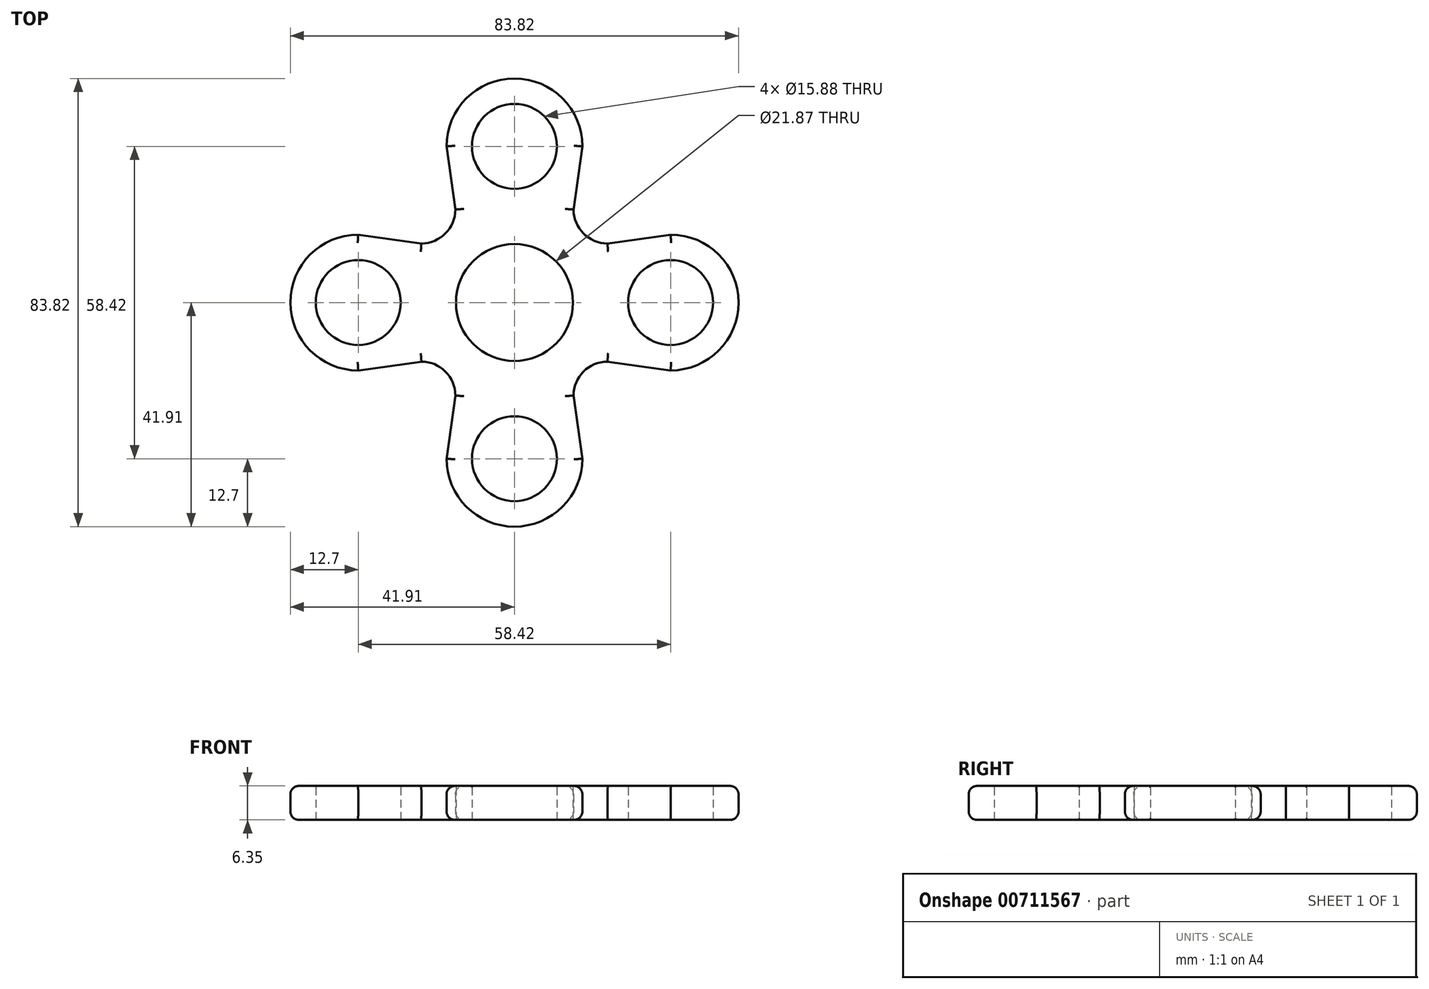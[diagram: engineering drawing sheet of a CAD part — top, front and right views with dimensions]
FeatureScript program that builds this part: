
annotation { "Feature Type Name" : "Feature", "Feature Type Description" : "" }
export const myFeature = defineFeature(function(context is Context, id is Id, definition is map)
    precondition{}
    {
        {
            var Q0;
            Q0=qCreatedBy(makeId("Top.planeOp"),FACE);
            var sketch = newSketch(context, id + "F0", { "sketchPlane" : qUnion([Q0])});
            skCircle(sketch, "E0", {"center": v(0, 0) * mm, "radius": 10.93 * mm});
            skLineSegment(sketch, "E1", {"start": v(0, 32.8) * mm, "end": v(0, -37.97) * mm, "construction": true});
            skLineSegment(sketch, "E2", {"start": v(-47.87, 0) * mm, "end": v(62.97, 0) * mm, "construction": true});
            skCircle(sketch, "E3", {"center": v(29.21, 0) * mm, "radius": 7.94 * mm});
            skCircle(sketch, "E4", {"center": v(0, 29.21) * mm, "radius": 7.94 * mm});
            skCircle(sketch, "E5", {"center": v(-29.21, 0) * mm, "radius": 7.94 * mm});
            skCircle(sketch, "E6", {"center": v(0, -29.21) * mm, "radius": 7.94 * mm});
            skArc(sketch, "E7", {"start": v(12.7, 29.2) * mm, "mid": v(0, 41.91) * mm, "end": v(-12.7, 29.21) * mm});
            skArc(sketch, "E8", {"start": v(29.2, -12.7) * mm, "mid": v(41.91, 0) * mm, "end": v(29.21, 12.7) * mm});
            skArc(sketch, "E9", {"start": v(-12.7, -29.21) * mm, "mid": v(0, -41.91) * mm, "end": v(12.7, -29.21) * mm});
            skArc(sketch, "E10", {"start": v(-29.21, 12.7) * mm, "mid": v(-41.91, 0) * mm, "end": v(-29.2, -12.7) * mm});
            skPoint(sketch, "E11.visualSharp", {"position": v(-11.05, 11.05) * mm});
            skArc(sketch, "E11.filletArc", {"start": v(-17.4, 11.05) * mm, "mid": v(-12.9, 12.9) * mm, "end": v(-11.05, 17.4) * mm});
            skPoint(sketch, "E12.visualSharp", {"position": v(11.05, 11.05) * mm});
            skArc(sketch, "E12.filletArc", {"start": v(11.05, 17.4) * mm, "mid": v(12.9, 12.9) * mm, "end": v(17.4, 11.05) * mm});
            skArc(sketch, "E13.MirrorCS", {"start": v(-17.4, -11.05) * mm, "mid": v(-12.9, -12.9) * mm, "end": v(-11.05, -17.4) * mm});
            skArc(sketch, "E14.MirrorCS", {"start": v(11.05, -17.4) * mm, "mid": v(12.9, -12.9) * mm, "end": v(17.4, -11.05) * mm});
            skLineSegment(sketch, "E15", {"start": v(-12.7, -29.21) * mm, "end": v(-11.05, -17.4) * mm});
            skLineSegment(sketch, "E16", {"start": v(12.7, -29.2) * mm, "end": v(11.05, -17.4) * mm});
            skLineSegment(sketch, "E17", {"start": v(17.4, -11.05) * mm, "end": v(29.2, -12.7) * mm});
            skLineSegment(sketch, "E18", {"start": v(17.4, 11.05) * mm, "end": v(29.2, 12.7) * mm});
            skLineSegment(sketch, "E19", {"start": v(11.05, 17.4) * mm, "end": v(12.7, 29.2) * mm});
            skLineSegment(sketch, "E20", {"start": v(-12.7, 29.21) * mm, "end": v(-11.05, 17.4) * mm});
            skLineSegment(sketch, "E21", {"start": v(-17.4, 11.05) * mm, "end": v(-29.21, 12.7) * mm});
            skLineSegment(sketch, "E22", {"start": v(-29.21, -12.7) * mm, "end": v(-17.4, -11.05) * mm});
            skSolve(sketch);
        }
        {
            var Q0;
            Q0 = qSketchRegion(id + "F0", true);
            extrude(context, id + "F1", {"entities" : qUnion([Q0]), "depth" : 6.35 * mm, "offsetDistance" : 25.4 * mm});
        }
        {
            var Q0;
            Q0=makeQuery(id+"F1.opExtrude","CAP_EDGE",EDGE,{"disambiguationData":[OSD([sQuery(id+"F0.wireOp",EDGE,"E10")])],"isStart":true});
            var Q1;
            Q1=makeQuery(id+"F1.opExtrude","CAP_EDGE",EDGE,{"disambiguationData":[OSD([sQuery(id+"F0.wireOp",EDGE,"E22")])],"isStart":true});
            var Q2;
            Q2=makeQuery(id+"F1.opExtrude","CAP_EDGE",EDGE,{"disambiguationData":[OSD([sQuery(id+"F0.wireOp",EDGE,"E13.MirrorCS")])],"isStart":true});
            var Q3;
            Q3=makeQuery(id+"F1.opExtrude","CAP_EDGE",EDGE,{"disambiguationData":[OSD([sQuery(id+"F0.wireOp",EDGE,"E15")])],"isStart":true});
            var Q4;
            Q4=makeQuery(id+"F1.opExtrude","CAP_EDGE",EDGE,{"disambiguationData":[OSD([sQuery(id+"F0.wireOp",EDGE,"E9")])],"isStart":true});
            var Q5;
            Q5=makeQuery(id+"F1.opExtrude","CAP_EDGE",EDGE,{"disambiguationData":[OSD([sQuery(id+"F0.wireOp",EDGE,"E16")])],"isStart":true});
            var Q6;
            Q6=makeQuery(id+"F1.opExtrude","CAP_EDGE",EDGE,{"disambiguationData":[OSD([sQuery(id+"F0.wireOp",EDGE,"E14.MirrorCS")])],"isStart":true});
            var Q7;
            Q7=makeQuery(id+"F1.opExtrude","CAP_EDGE",EDGE,{"disambiguationData":[OSD([sQuery(id+"F0.wireOp",EDGE,"E17")])],"isStart":true});
            var Q8;
            Q8=makeQuery(id+"F1.opExtrude","CAP_EDGE",EDGE,{"disambiguationData":[OSD([sQuery(id+"F0.wireOp",EDGE,"E8")])],"isStart":true});
            var Q9;
            Q9=makeQuery(id+"F1.opExtrude","CAP_EDGE",EDGE,{"disambiguationData":[OSD([sQuery(id+"F0.wireOp",EDGE,"E18")])],"isStart":true});
            var Q10;
            Q10=makeQuery(id+"F1.opExtrude","CAP_EDGE",EDGE,{"disambiguationData":[OSD([sQuery(id+"F0.wireOp",EDGE,"E12.filletArc")])],"isStart":true});
            var Q11;
            Q11=makeQuery(id+"F1.opExtrude","CAP_EDGE",EDGE,{"disambiguationData":[OSD([sQuery(id+"F0.wireOp",EDGE,"E19")])],"isStart":true});
            var Q12;
            Q12=makeQuery(id+"F1.opExtrude","CAP_EDGE",EDGE,{"disambiguationData":[OSD([sQuery(id+"F0.wireOp",EDGE,"E7")])],"isStart":true});
            var Q13;
            Q13=makeQuery(id+"F1.opExtrude","CAP_EDGE",EDGE,{"disambiguationData":[OSD([sQuery(id+"F0.wireOp",EDGE,"E20")])],"isStart":true});
            var Q14;
            Q14=makeQuery(id+"F1.opExtrude","CAP_EDGE",EDGE,{"disambiguationData":[OSD([sQuery(id+"F0.wireOp",EDGE,"E11.filletArc")])],"isStart":true});
            var Q15;
            Q15=makeQuery(id+"F1.opExtrude","CAP_EDGE",EDGE,{"disambiguationData":[OSD([sQuery(id+"F0.wireOp",EDGE,"E21")])],"isStart":true});
            var Q16;
            Q16=makeQuery(id+"F1.opExtrude","CAP_EDGE",EDGE,{"disambiguationData":[OSD([sQuery(id+"F0.wireOp",EDGE,"E10")])],"isStart":false});
            var Q17;
            Q17=makeQuery(id+"F1.opExtrude","CAP_EDGE",EDGE,{"disambiguationData":[OSD([sQuery(id+"F0.wireOp",EDGE,"E22")])],"isStart":false});
            var Q18;
            Q18=makeQuery(id+"F1.opExtrude","CAP_EDGE",EDGE,{"disambiguationData":[OSD([sQuery(id+"F0.wireOp",EDGE,"E13.MirrorCS")])],"isStart":false});
            var Q19;
            Q19=makeQuery(id+"F1.opExtrude","CAP_EDGE",EDGE,{"disambiguationData":[OSD([sQuery(id+"F0.wireOp",EDGE,"E21")])],"isStart":false});
            var Q20;
            Q20=makeQuery(id+"F1.opExtrude","CAP_EDGE",EDGE,{"disambiguationData":[OSD([sQuery(id+"F0.wireOp",EDGE,"E11.filletArc")])],"isStart":false});
            var Q21;
            Q21=makeQuery(id+"F1.opExtrude","CAP_EDGE",EDGE,{"disambiguationData":[OSD([sQuery(id+"F0.wireOp",EDGE,"E20")])],"isStart":false});
            var Q22;
            Q22=makeQuery(id+"F1.opExtrude","CAP_EDGE",EDGE,{"disambiguationData":[OSD([sQuery(id+"F0.wireOp",EDGE,"E7")])],"isStart":false});
            var Q23;
            Q23=makeQuery(id+"F1.opExtrude","CAP_EDGE",EDGE,{"disambiguationData":[OSD([sQuery(id+"F0.wireOp",EDGE,"E19")])],"isStart":false});
            var Q24;
            Q24=makeQuery(id+"F1.opExtrude","CAP_EDGE",EDGE,{"disambiguationData":[OSD([sQuery(id+"F0.wireOp",EDGE,"E8")])],"isStart":false});
            var Q25;
            Q25=makeQuery(id+"F1.opExtrude","CAP_EDGE",EDGE,{"disambiguationData":[OSD([sQuery(id+"F0.wireOp",EDGE,"E17")])],"isStart":false});
            var Q26;
            Q26=makeQuery(id+"F1.opExtrude","CAP_EDGE",EDGE,{"disambiguationData":[OSD([sQuery(id+"F0.wireOp",EDGE,"E14.MirrorCS")])],"isStart":false});
            var Q27;
            Q27=makeQuery(id+"F1.opExtrude","CAP_EDGE",EDGE,{"disambiguationData":[OSD([sQuery(id+"F0.wireOp",EDGE,"E16")])],"isStart":false});
            var Q28;
            Q28=makeQuery(id+"F1.opExtrude","CAP_EDGE",EDGE,{"disambiguationData":[OSD([sQuery(id+"F0.wireOp",EDGE,"E9")])],"isStart":false});
            var Q29;
            Q29=makeQuery(id+"F1.opExtrude","CAP_EDGE",EDGE,{"disambiguationData":[OSD([sQuery(id+"F0.wireOp",EDGE,"E15")])],"isStart":false});
            var Q30;
            Q30=makeQuery(id+"F1.opExtrude","CAP_EDGE",EDGE,{"disambiguationData":[OSD([sQuery(id+"F0.wireOp",EDGE,"E12.filletArc")])],"isStart":false});
            var Q31;
            Q31=makeQuery(id+"F1.opExtrude","CAP_EDGE",EDGE,{"disambiguationData":[OSD([sQuery(id+"F0.wireOp",EDGE,"E18")])],"isStart":false});
            fillet(context, id + "F2", {"entities" : qUnion([Q0, Q1, Q2, Q3, Q4, Q5, Q6, Q7, Q8, Q9, Q10, Q11, Q12, Q13, Q14, Q15, Q16, Q17, Q18, Q19, Q20, Q21, Q22, Q23, Q24, Q25, Q26, Q27, Q28, Q29, Q30, Q31]), "radius" : 1.57 * mm, "allowEdgeOverflow" : false});
        }
        {
            var Q0;
            Q0=makeQuery(id+"F1.opExtrude","CAP_EDGE",EDGE,{"disambiguationData":[OSD([sQuery(id+"F0.wireOp",EDGE,"E5")])],"isStart":false});
            var Q1;
            Q1=makeQuery(id+"F1.opExtrude","CAP_EDGE",EDGE,{"disambiguationData":[OSD([sQuery(id+"F0.wireOp",EDGE,"E4")])],"isStart":false});
            var Q2;
            Q2=makeQuery(id+"F1.opExtrude","CAP_EDGE",EDGE,{"disambiguationData":[OSD([sQuery(id+"F0.wireOp",EDGE,"E0")])],"isStart":false});
            var Q3;
            Q3=makeQuery(id+"F1.opExtrude","CAP_EDGE",EDGE,{"disambiguationData":[OSD([sQuery(id+"F0.wireOp",EDGE,"E3")])],"isStart":false});
            var Q4;
            Q4=makeQuery(id+"F1.opExtrude","CAP_EDGE",EDGE,{"disambiguationData":[OSD([sQuery(id+"F0.wireOp",EDGE,"E6")])],"isStart":false});
            var Q5;
            Q5=makeQuery(id+"F1.opExtrude","CAP_EDGE",EDGE,{"disambiguationData":[OSD([sQuery(id+"F0.wireOp",EDGE,"E6")])],"isStart":true});
            var Q6;
            Q6=makeQuery(id+"F1.opExtrude","CAP_EDGE",EDGE,{"disambiguationData":[OSD([sQuery(id+"F0.wireOp",EDGE,"E5")])],"isStart":true});
            var Q7;
            Q7=makeQuery(id+"F1.opExtrude","CAP_EDGE",EDGE,{"disambiguationData":[OSD([sQuery(id+"F0.wireOp",EDGE,"E0")])],"isStart":true});
            var Q8;
            Q8=makeQuery(id+"F1.opExtrude","CAP_EDGE",EDGE,{"disambiguationData":[OSD([sQuery(id+"F0.wireOp",EDGE,"E3")])],"isStart":true});
            var Q9;
            Q9=makeQuery(id+"F1.opExtrude","CAP_EDGE",EDGE,{"disambiguationData":[OSD([sQuery(id+"F0.wireOp",EDGE,"E4")])],"isStart":true});
            fillet(context, id + "F3", {"entities" : qUnion([Q0, Q1, Q2, Q3, Q4, Q5, Q6, Q7, Q8, Q9]), "radius" : 0.25 * mm, "tangentPropagation" : true, "allowEdgeOverflow" : false});
        }
    });
